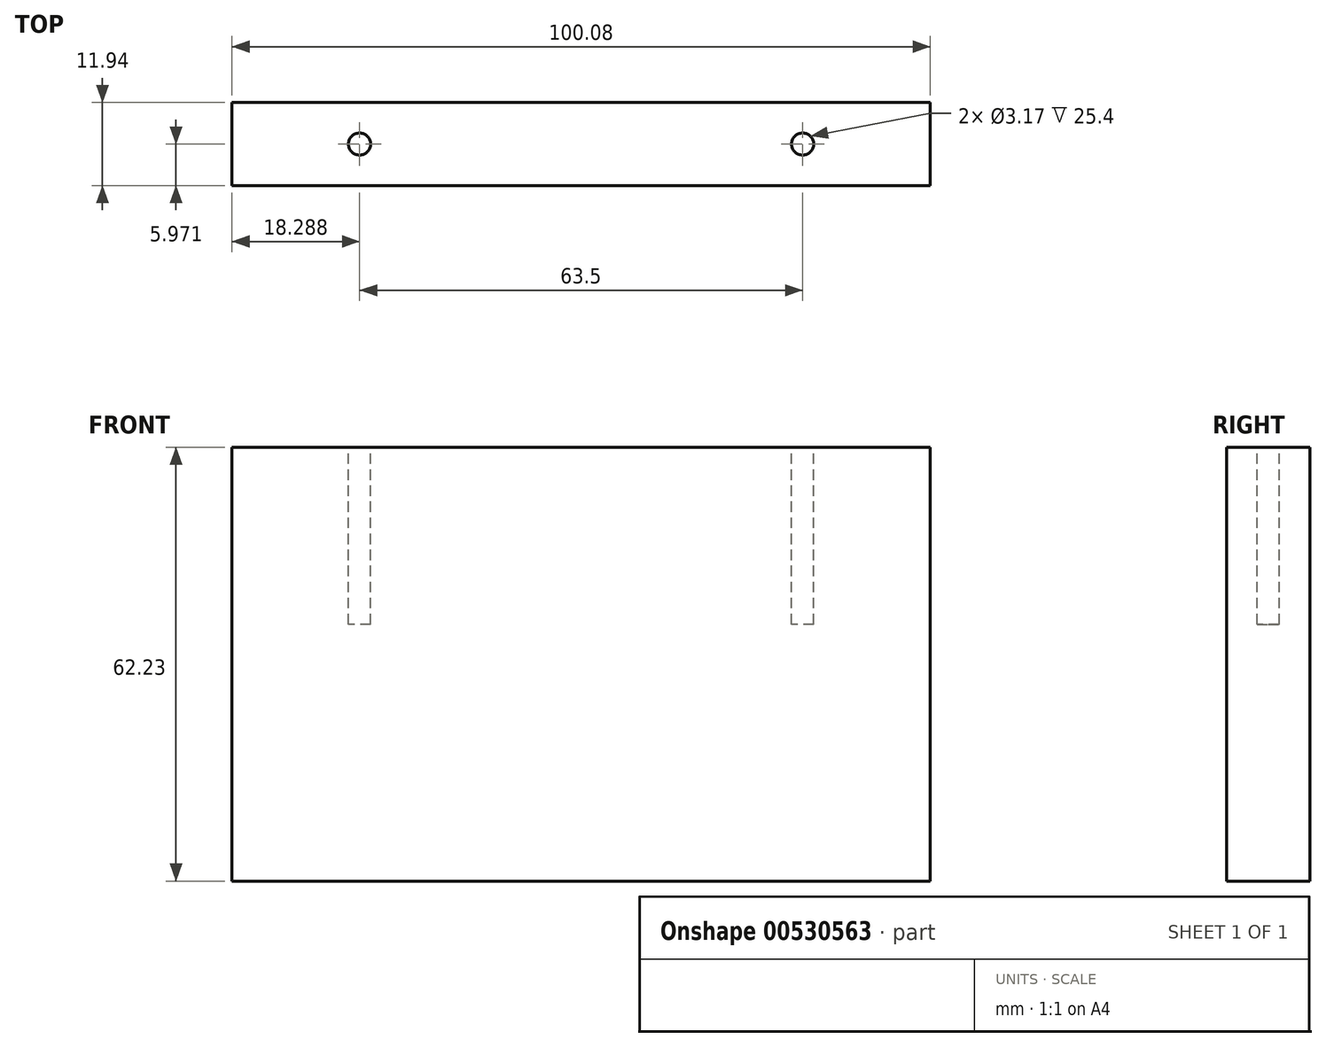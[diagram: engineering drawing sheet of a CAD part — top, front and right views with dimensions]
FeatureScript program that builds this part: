
annotation { "Feature Type Name" : "Feature", "Feature Type Description" : "" }
export const myFeature = defineFeature(function(context is Context, id is Id, definition is map)
    precondition{}
    {
        {
            var Q0;
            Q0=qCreatedBy(makeId("Front.planeOp"),FACE);
            var sketch = newSketch(context, id + "F0", { "sketchPlane" : qUnion([Q0])});
            skLineSegment(sketch, "E0.bottom", {"start": v(0, 0) * mm, "end": v(100.08, 0) * mm});
            skLineSegment(sketch, "E0.top", {"start": v(0, 62.23) * mm, "end": v(100.08, 62.23) * mm});
            skLineSegment(sketch, "E0.left", {"start": v(0, 0) * mm, "end": v(0, 62.23) * mm});
            skLineSegment(sketch, "E0.right", {"start": v(100.08, 0) * mm, "end": v(100.08, 62.23) * mm});
            skSolve(sketch);
        }
        {
            var Q0;
            Q0 = qSketchRegion(id + "F0", true);
            extrude(context, id + "F1", {"entities" : qUnion([Q0]), "depth" : 11.94 * mm, "offsetDistance" : 25.4 * mm});
        }
        {
            var Q0;
            Q0=makeQuery(id+"F1.opExtrude","SWEPT_FACE",FACE,{"disambiguationData":[OSD([sQuery(id+"F0.wireOp",EDGE,"E0.top")])]});
            var sketch = newSketch(context, id + "F2", { "sketchPlane" : qUnion([Q0])});
            skCircle(sketch, "E1", {"center": v(18.29, -5.97) * mm, "radius": 1.59 * mm});
            skCircle(sketch, "E2", {"center": v(81.79, -5.97) * mm, "radius": 1.59 * mm});
            skSolve(sketch);
        }
        {
            var Q0;
            Q0 = qSketchRegion(id + "F2", true);
            extrude(context, id + "F3", {"entities" : qUnion([Q0]), "operationType" : NewBodyOperationType.REMOVE, "oppositeDirection" : true, "depth" : 25.4 * mm, "offsetDistance" : 25.4 * mm});
        }
    });
